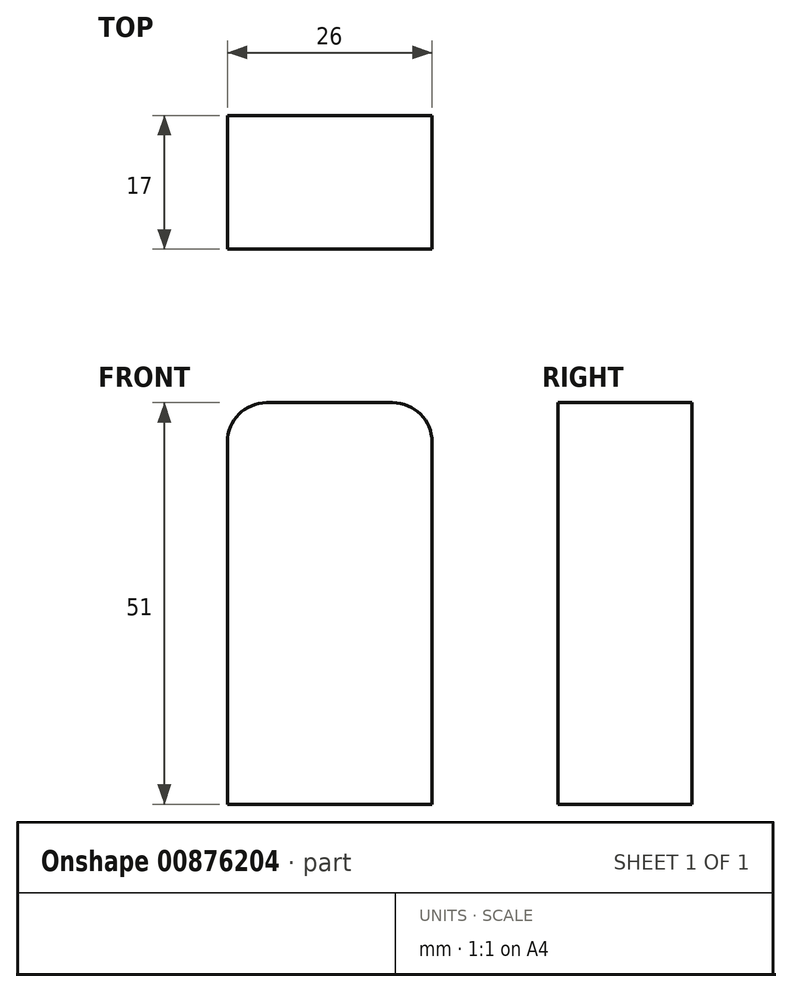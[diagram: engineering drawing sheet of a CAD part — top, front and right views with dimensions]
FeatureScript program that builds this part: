
annotation { "Feature Type Name" : "Feature", "Feature Type Description" : "" }
export const myFeature = defineFeature(function(context is Context, id is Id, definition is map)
    precondition{}
    {
        {
            var Q0;
            Q0=qCreatedBy(makeId("Front.planeOp"),FACE);
            var sketch = newSketch(context, id + "F0", { "sketchPlane" : qUnion([Q0])});
            skLineSegment(sketch, "E0.bottom", {"start": v(13, 25.5) * mm, "end": v(-13, 25.5) * mm});
            skLineSegment(sketch, "E0.top", {"start": v(13, -25.5) * mm, "end": v(-13, -25.5) * mm});
            skLineSegment(sketch, "E0.left", {"start": v(13, 25.5) * mm, "end": v(13, -25.5) * mm});
            skLineSegment(sketch, "E0.right", {"start": v(-13, 25.5) * mm, "end": v(-13, -25.5) * mm});
            skPoint(sketch, "E0.middle", {"position": v(0, 0) * mm});
            skSolve(sketch);
        }
        {
            var Q0;
            Q0=qSketchRegion(id+"F0",true);
            extrude(context, id + "F1", {"entities" : qUnion([Q0]), "depth" : 17 * mm, "offsetDistance" : 25 * mm});
        }
        {
            var Q0;
            Q0=makeQuery(id+"F1.opExtrude","SWEPT_EDGE",EDGE,{"disambiguationData":[OSD([sQuery(id+"F0.wireOp",EDGE,"E0.bottom"),sQuery(id+"F0.wireOp",EDGE,"E0.left")])]});
            var Q1;
            Q1=makeQuery(id+"F1.opExtrude","SWEPT_EDGE",EDGE,{"disambiguationData":[OSD([sQuery(id+"F0.wireOp",EDGE,"E0.bottom"),sQuery(id+"F0.wireOp",EDGE,"E0.right")])]});
            fillet(context, id + "F2", {"entities" : qUnion([Q0, Q1]), "radius" : 5 * mm, "tangentPropagation" : true, "allowEdgeOverflow" : false});
        }
    });
